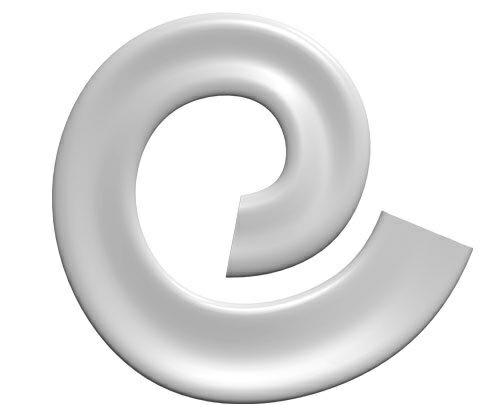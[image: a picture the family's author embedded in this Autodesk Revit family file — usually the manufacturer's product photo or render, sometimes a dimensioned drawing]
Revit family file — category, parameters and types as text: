
# Revit family: CITY ALPHABET letter „E”
name_source: partatom
category: Furniture
revit_build: Autodesk Revit 2018 (Build: 20190510_1515(x64)
units: mm (PartAtom-declared; Revit-internal decimal feet)

## family parameters
Cut with Voids When Loaded = No
Host = Face
OmniClass Number = 23.40.10.11.14
OmniClass Title = Exterior Seating
Room Calculation Point = No
Shared = No

## types (1)
- CITY ALPHABET letter „E”
    Default Elevation = 1219 mm
    Height = 510 mm  [stored 1.67323 ft]
    IfcExportAs = IfcFurnishingElement
    Length = 1890 mm  [stored 6.20079 ft]
    Manufacturer = Astrini Design
    Material information = Colour choice from RAL colour standard. Customer may inquire about specific request regarding individual order.
    Model = CITY ALPHABET letter „E”
    Operating temperature = -40°C to 80°C, ( -40°F to 176°F )
    Type Comments = Bench
    Type Image = E.jpg
    URL = https://astrini-design.pl
    Weight (approximately) = 75.00 kg
    Weight - filled (approximately) = 125.00 kg
    Width = 2030 mm  [stored 6.6601 ft]

note: [stored X ft] marks values corroborated as IEEE doubles in the binary element streams (Revit-internal decimal feet)
